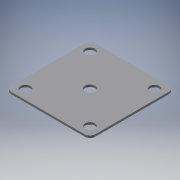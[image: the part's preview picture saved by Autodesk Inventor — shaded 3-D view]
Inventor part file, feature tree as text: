
AUTODESK INVENTOR PART (.ipt)
format: ipt  version: 2019 (Build 230136000, 136)  size: 124,928 bytes
history: native  units: mm
features: other x1, extrude x1, sketch x1
ambient origin geometry x8: Origin, YZ Plane, XZ Plane, XY Plane, X Axis, Y Axis, Z Axis, Center Point
bodies: Body1 (feature_tree)
feature tree (3):
  other  "솔리드1"
  extrude  "돌출1"  Depth=82.0mm
  sketch  "스케치1"
